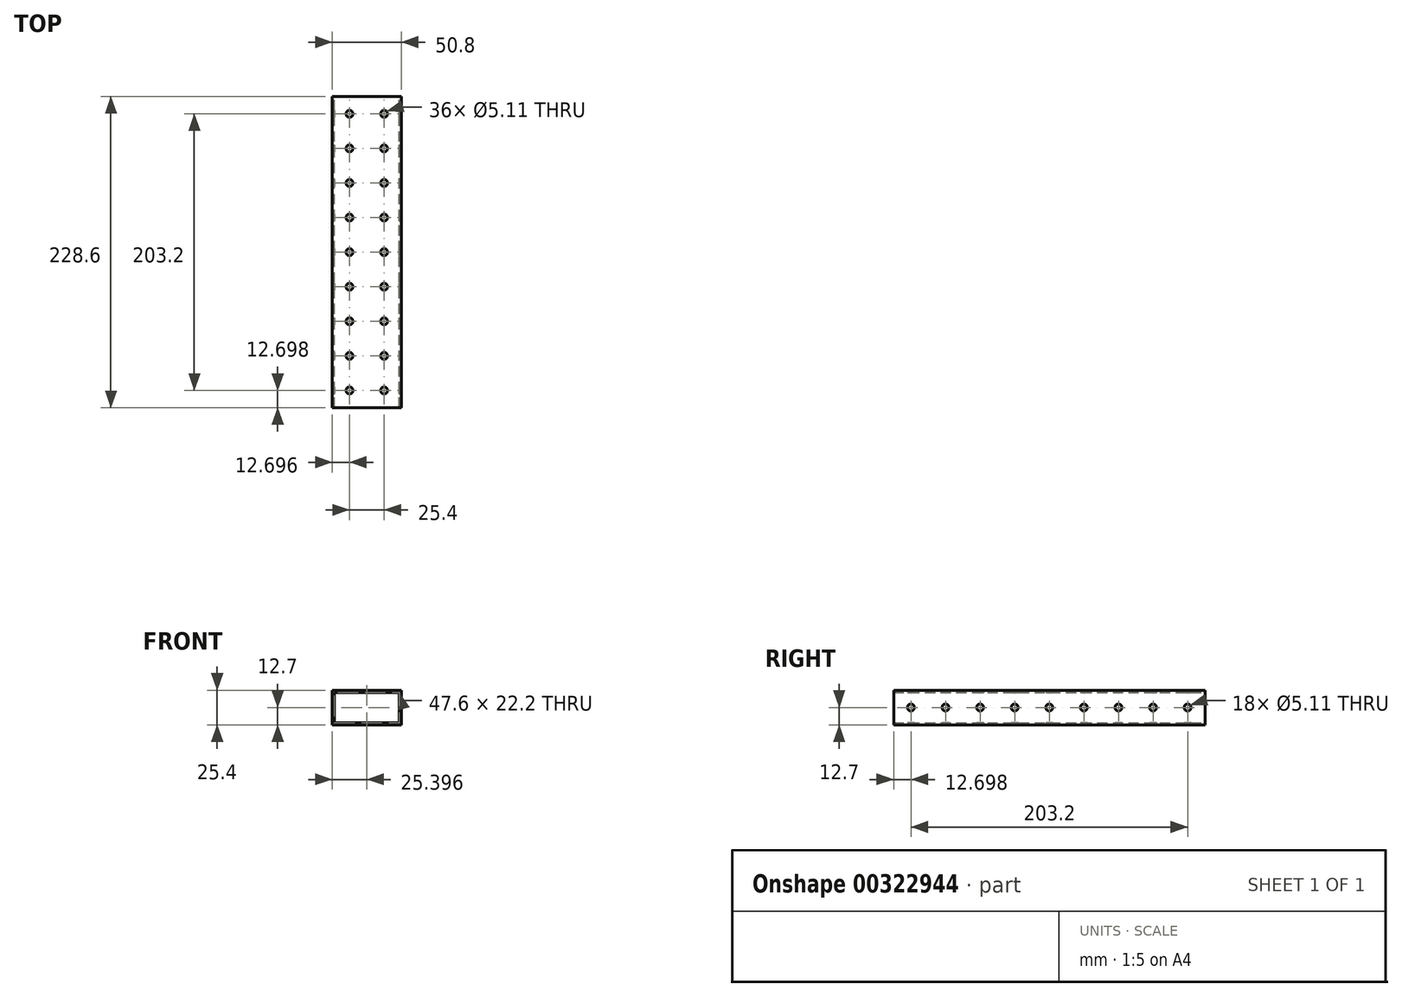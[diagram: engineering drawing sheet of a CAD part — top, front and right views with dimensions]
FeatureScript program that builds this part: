
annotation { "Feature Type Name" : "Feature", "Feature Type Description" : "" }
export const myFeature = defineFeature(function(context is Context, id is Id, definition is map)
    precondition{}
    {
        {
            var Q0;
            Q0=qCreatedBy(makeId("Top.planeOp"),FACE);
            var sketch = newSketch(context, id + "F0", { "sketchPlane" : qUnion([Q0])});
            skLineSegment(sketch, "E0.bottom", {"start": v(-103.11, 153.68) * mm, "end": v(-52.31, 153.68) * mm});
            skLineSegment(sketch, "E0.top", {"start": v(-103.11, -74.92) * mm, "end": v(-52.31, -74.92) * mm});
            skLineSegment(sketch, "E0.left", {"start": v(-103.11, 153.68) * mm, "end": v(-103.11, -74.92) * mm});
            skLineSegment(sketch, "E0.right", {"start": v(-52.31, 153.68) * mm, "end": v(-52.31, -74.92) * mm});
            skSolve(sketch);
        }
        {
            var Q0;
            Q0=makeQuery(id+"F0.imprint","IMPRINT",FACE,{"disambiguationData":[TD([[makeQuery(id+"F0.imprint","IMPRINT",EDGE,{"derivedFrom":sQuery(id+"F0.wireOp",EDGE,"E0.bottom")}),-1.0]])]});
            extrude(context, id + "F1", {"entities" : qUnion([Q0]), "depth" : 25.4 * mm});
        }
        {
            var Q0;
            Q0=makeQuery(id+"F1.opExtrude","SWEPT_FACE",FACE,{"disambiguationData":[OSD([sQuery(id+"F0.wireOp",EDGE,"E0.bottom")])]});
            var sketch = newSketch(context, id + "F2", { "sketchPlane" : qUnion([Q0])});
            skLineSegment(sketch, "E1.bottom", {"start": v(53.91, 23.8) * mm, "end": v(101.51, 23.8) * mm});
            skLineSegment(sketch, "E1.top", {"start": v(53.91, 1.6) * mm, "end": v(101.51, 1.6) * mm});
            skLineSegment(sketch, "E1.left", {"start": v(53.91, 23.8) * mm, "end": v(53.91, 1.6) * mm});
            skLineSegment(sketch, "E1.right", {"start": v(101.51, 23.8) * mm, "end": v(101.51, 1.6) * mm});
            skSolve(sketch);
        }
        {
            var Q0;
            Q0=makeQuery(id+"F2.imprint","IMPRINT",FACE,{"disambiguationData":[TD([[makeQuery(id+"F2.imprint","IMPRINT",EDGE,{"derivedFrom":sQuery(id+"F2.wireOp",EDGE,"E1.bottom")}),-1.0]])]});
            extrude(context, id + "F3", {"entities" : qUnion([Q0]), "operationType" : NewBodyOperationType.REMOVE, "endBound" : BoundingType.THROUGH_ALL, "oppositeDirection" : true, "depth" : 25.4 * mm});
        }
        {
            var Q0;
            Q0=makeQuery(id+"F1.opExtrude","CAP_FACE",FACE,{"disambiguationData":[OSD([sQuery(id+"F0.wireOp",EDGE,"E0.bottom"),sQuery(id+"F0.wireOp",EDGE,"E0.top"),sQuery(id+"F0.wireOp",EDGE,"E0.left"),sQuery(id+"F0.wireOp",EDGE,"E0.right")])],"isStart":false});
            var sketch = newSketch(context, id + "F4", { "sketchPlane" : qUnion([Q0])});
            skCircle(sketch, "E2", {"center": v(-90.41, 140.98) * mm, "radius": 2.55 * mm});
            skCircle(sketch, "E3.0.1.0", {"center": v(-90.41, 115.58) * mm, "radius": 2.55 * mm});
            skCircle(sketch, "E3.0.2.0", {"center": v(-90.41, 90.18) * mm, "radius": 2.55 * mm});
            skCircle(sketch, "E3.0.3.0", {"center": v(-90.41, 64.78) * mm, "radius": 2.55 * mm});
            skCircle(sketch, "E3.0.4.0", {"center": v(-90.41, 39.38) * mm, "radius": 2.55 * mm});
            skCircle(sketch, "E3.0.5.0", {"center": v(-90.41, 13.98) * mm, "radius": 2.55 * mm});
            skCircle(sketch, "E3.0.6.0", {"center": v(-90.41, -11.42) * mm, "radius": 2.55 * mm});
            skCircle(sketch, "E3.0.7.0", {"center": v(-90.41, -36.82) * mm, "radius": 2.55 * mm});
            skCircle(sketch, "E3.0.8.0", {"center": v(-90.41, -62.22) * mm, "radius": 2.55 * mm});
            skCircle(sketch, "E3.1.0.0", {"center": v(-65.01, 140.98) * mm, "radius": 2.55 * mm});
            skCircle(sketch, "E3.1.1.0", {"center": v(-65.01, 115.58) * mm, "radius": 2.55 * mm});
            skCircle(sketch, "E3.1.2.0", {"center": v(-65.01, 90.18) * mm, "radius": 2.55 * mm});
            skCircle(sketch, "E3.1.3.0", {"center": v(-65.01, 64.78) * mm, "radius": 2.55 * mm});
            skCircle(sketch, "E3.1.4.0", {"center": v(-65.01, 39.38) * mm, "radius": 2.55 * mm});
            skCircle(sketch, "E3.1.5.0", {"center": v(-65.01, 13.98) * mm, "radius": 2.55 * mm});
            skCircle(sketch, "E3.1.6.0", {"center": v(-65.01, -11.42) * mm, "radius": 2.55 * mm});
            skCircle(sketch, "E3.1.7.0", {"center": v(-65.01, -36.82) * mm, "radius": 2.55 * mm});
            skCircle(sketch, "E3.1.8.0", {"center": v(-65.01, -62.22) * mm, "radius": 2.55 * mm});
            skLineSegment(sketch, "E3.direction1", {"start": v(-90.41, 140.98) * mm, "end": v(-65.01, 140.98) * mm, "construction": true});
            skLineSegment(sketch, "E3.direction2", {"start": v(-90.41, 140.98) * mm, "end": v(-90.41, 115.58) * mm, "construction": true});
            skSolve(sketch);
        }
        {
            var Q0;
            Q0=sQuery(id+"F4.wireOp",VERTEX,"E3.1.4.0.center");
            var Q1;
            Q1=sQuery(id+"F4.wireOp",VERTEX,"E3.1.7.0.center");
            var Q2;
            Q2=sQuery(id+"F4.wireOp",VERTEX,"E3.1.5.0.center");
            var Q3;
            Q3=sQuery(id+"F4.wireOp",VERTEX,"E3.1.1.0.center");
            var Q4;
            Q4=sQuery(id+"F4.wireOp",VERTEX,"E3.1.2.0.center");
            var Q5;
            Q5=sQuery(id+"F4.wireOp",VERTEX,"E3.direction1.end");
            var Q6;
            Q6=sQuery(id+"F4.wireOp",VERTEX,"E3.1.3.0.center");
            var Q7;
            Q7=sQuery(id+"F4.wireOp",VERTEX,"E2.center");
            var Q8;
            Q8=sQuery(id+"F4.wireOp",VERTEX,"E3.0.1.0.center");
            var Q9;
            Q9=sQuery(id+"F4.wireOp",VERTEX,"E3.0.2.0.center");
            var Q10;
            Q10=sQuery(id+"F4.wireOp",VERTEX,"E3.0.3.0.center");
            var Q11;
            Q11=sQuery(id+"F4.wireOp",VERTEX,"E3.0.4.0.center");
            var Q12;
            Q12=sQuery(id+"F4.wireOp",VERTEX,"E3.0.5.0.center");
            var Q13;
            Q13=sQuery(id+"F4.wireOp",VERTEX,"E3.0.6.0.center");
            var Q14;
            Q14=sQuery(id+"F4.wireOp",VERTEX,"E3.0.7.0.center");
            var Q15;
            Q15=sQuery(id+"F4.wireOp",VERTEX,"E3.1.8.0.center");
            var Q16;
            Q16=sQuery(id+"F4.wireOp",VERTEX,"E3.0.8.0.center");
            var Q17;
            Q17=sQuery(id+"F4.wireOp",VERTEX,"E3.1.6.0.center");
            var Q18;
            Q18=makeQuery(id+"F1.opExtrude","SWEPT_BODY",BODY,{"disambiguationData":[OSD([sQuery(id+"F0.wireOp",EDGE,"E0.bottom"),sQuery(id+"F0.wireOp",EDGE,"E0.top"),sQuery(id+"F0.wireOp",EDGE,"E0.left"),sQuery(id+"F0.wireOp",EDGE,"E0.right")])]});
            hole(context, id + "F5", {"style" : HoleStyle.SIMPLE, "endStyle" : HoleEndStyle.THROUGH, "holeDiameter" : 5.1 * mm, "tappedDepth" : 12.7 * mm, "tapClearance" : 3, "locations" : qUnion([Q0, Q1, Q2, Q3, Q4, Q5, Q6, Q7, Q8, Q9, Q10, Q11, Q12, Q13, Q14, Q15, Q16, Q17]), "scope" : qUnion([Q18])});
        }
        {
            var Q0;
            Q0=makeQuery(id+"F1.opExtrude","SWEPT_FACE",FACE,{"disambiguationData":[OSD([sQuery(id+"F0.wireOp",EDGE,"E0.left")])]});
            var sketch = newSketch(context, id + "F6", { "sketchPlane" : qUnion([Q0])});
            skCircle(sketch, "E4", {"center": v(-140.98, 12.7) * mm, "radius": 2.55 * mm});
            skCircle(sketch, "E5.1.0.0", {"center": v(-115.58, 12.7) * mm, "radius": 2.55 * mm});
            skCircle(sketch, "E5.2.0.0", {"center": v(-90.18, 12.7) * mm, "radius": 2.55 * mm});
            skCircle(sketch, "E5.3.0.0", {"center": v(-64.78, 12.7) * mm, "radius": 2.55 * mm});
            skCircle(sketch, "E5.4.0.0", {"center": v(-39.38, 12.7) * mm, "radius": 2.55 * mm});
            skCircle(sketch, "E5.5.0.0", {"center": v(-13.98, 12.7) * mm, "radius": 2.55 * mm});
            skCircle(sketch, "E5.6.0.0", {"center": v(11.42, 12.7) * mm, "radius": 2.55 * mm});
            skCircle(sketch, "E5.7.0.0", {"center": v(36.82, 12.7) * mm, "radius": 2.55 * mm});
            skCircle(sketch, "E5.8.0.0", {"center": v(62.22, 12.7) * mm, "radius": 2.55 * mm});
            skLineSegment(sketch, "E5.direction1", {"start": v(-140.98, 12.7) * mm, "end": v(-115.58, 12.7) * mm, "construction": true});
            skSolve(sketch);
        }
        {
            var Q0;
            Q0=sQuery(id+"F6.wireOp",VERTEX,"E4.center");
            var Q1;
            Q1=sQuery(id+"F6.wireOp",VERTEX,"E5.2.0.0.center");
            var Q2;
            Q2=sQuery(id+"F6.wireOp",VERTEX,"E5.1.0.0.center");
            var Q3;
            Q3=sQuery(id+"F6.wireOp",VERTEX,"E5.4.0.0.center");
            var Q4;
            Q4=sQuery(id+"F6.wireOp",VERTEX,"E5.3.0.0.center");
            var Q5;
            Q5=sQuery(id+"F6.wireOp",VERTEX,"E5.6.0.0.center");
            var Q6;
            Q6=sQuery(id+"F6.wireOp",VERTEX,"E5.5.0.0.center");
            var Q7;
            Q7=sQuery(id+"F6.wireOp",VERTEX,"E5.8.0.0.center");
            var Q8;
            Q8=sQuery(id+"F6.wireOp",VERTEX,"E5.7.0.0.center");
            var Q9;
            Q9=makeQuery(id+"F1.opExtrude","SWEPT_BODY",BODY,{"disambiguationData":[OSD([sQuery(id+"F0.wireOp",EDGE,"E0.bottom"),sQuery(id+"F0.wireOp",EDGE,"E0.top"),sQuery(id+"F0.wireOp",EDGE,"E0.left"),sQuery(id+"F0.wireOp",EDGE,"E0.right")])]});
            hole(context, id + "F7", {"style" : HoleStyle.SIMPLE, "endStyle" : HoleEndStyle.THROUGH, "holeDiameter" : 5.1 * mm, "tappedDepth" : 12.7 * mm, "tapClearance" : 3, "locations" : qUnion([Q0, Q1, Q2, Q3, Q4, Q5, Q6, Q7, Q8]), "scope" : qUnion([Q9])});
        }
    });
